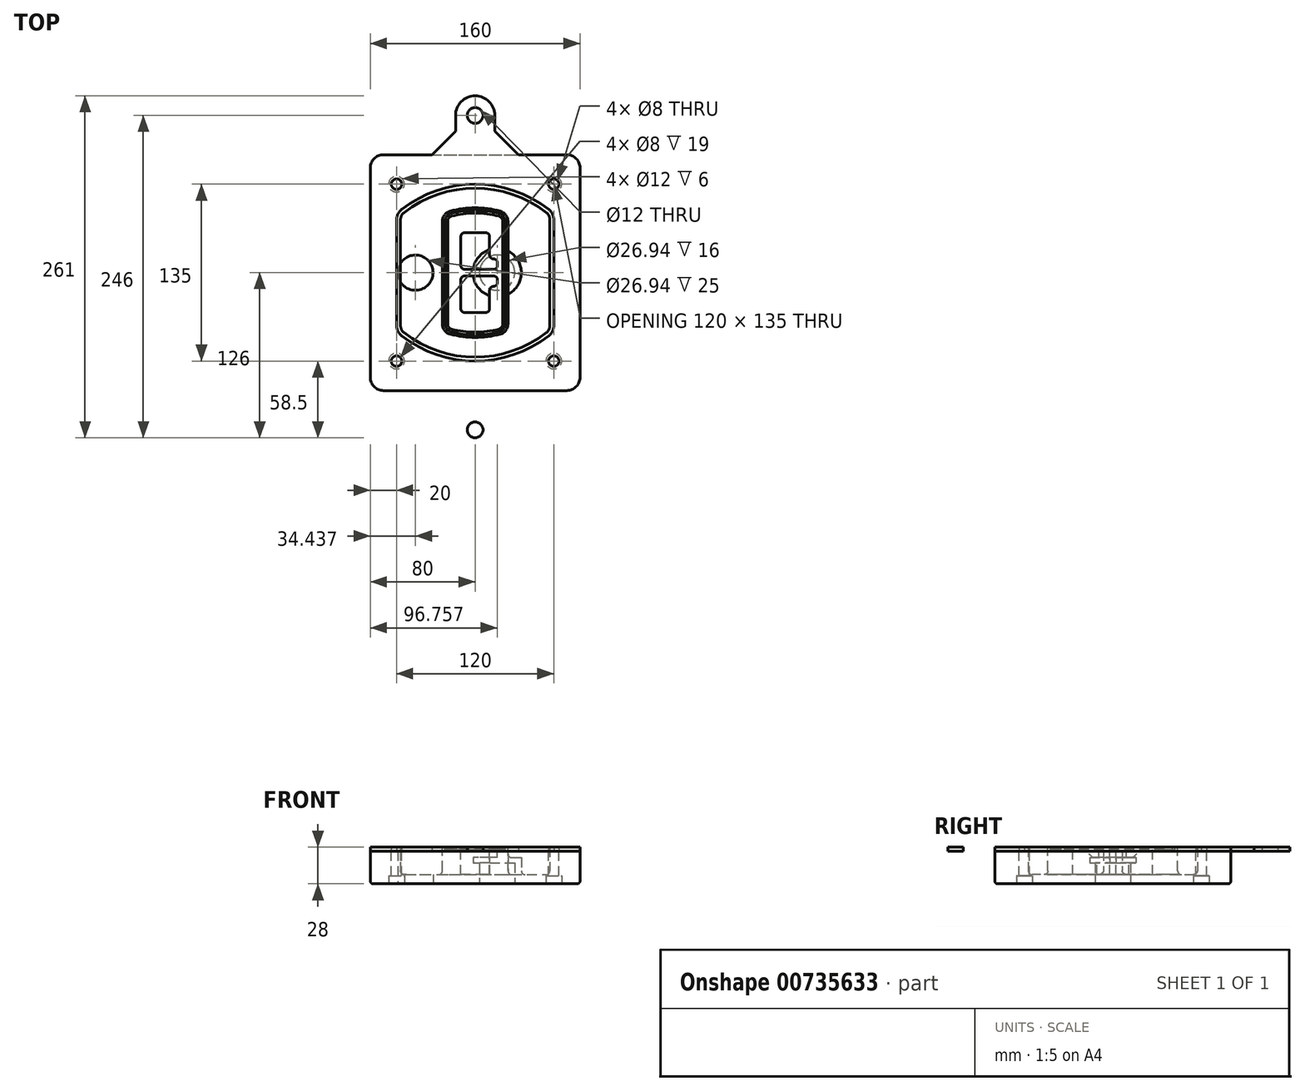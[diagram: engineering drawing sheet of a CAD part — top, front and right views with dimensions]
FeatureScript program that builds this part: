
annotation { "Feature Type Name" : "Feature", "Feature Type Description" : "" }
export const myFeature = defineFeature(function(context is Context, id is Id, definition is map)
    precondition{}
    {
        {
            var Q0;
            Q0=qCreatedBy(makeId("Top.planeOp"),FACE);
            var sketch = newSketch(context, id + "F0", { "sketchPlane" : qUnion([Q0])});
            skPoint(sketch, "E0.rect.middle", {"position": v(0, 0) * mm});
            skLineSegment(sketch, "E1.bottom", {"start": v(-70, -90) * mm, "end": v(70, -90) * mm});
            skLineSegment(sketch, "E1.top", {"start": v(-70, 90) * mm, "end": v(70, 90) * mm});
            skLineSegment(sketch, "E1.left", {"start": v(-80, -80) * mm, "end": v(-80, 80) * mm});
            skLineSegment(sketch, "E1.right", {"start": v(80, -80) * mm, "end": v(80, 80) * mm});
            skLineSegment(sketch, "E2", {"start": v(-80, 90) * mm, "end": v(80, -90) * mm, "construction": true});
            skLineSegment(sketch, "E3", {"start": v(80, 90) * mm, "end": v(-80, -90) * mm, "construction": true});
            skCircle(sketch, "E4", {"center": v(-60, 67.5) * mm, "radius": 4 * mm});
            skCircle(sketch, "E5", {"center": v(60, 67.5) * mm, "radius": 4 * mm});
            skCircle(sketch, "E6", {"center": v(60, -67.5) * mm, "radius": 4 * mm});
            skCircle(sketch, "E7", {"center": v(-60, -67.5) * mm, "radius": 4 * mm});
            skLineSegment(sketch, "E8", {"start": v(-60, 67.5) * mm, "end": v(60, 67.5) * mm, "construction": true});
            skLineSegment(sketch, "E9", {"start": v(60, 67.5) * mm, "end": v(60, -67.5) * mm, "construction": true});
            skLineSegment(sketch, "E10", {"start": v(60, -67.5) * mm, "end": v(-60, -67.5) * mm, "construction": true});
            skLineSegment(sketch, "E11", {"start": v(-60, -67.5) * mm, "end": v(-60, 67.5) * mm, "construction": true});
            skLineSegment(sketch, "E12", {"start": v(-60, 40.3) * mm, "end": v(-60, -40.3) * mm});
            skLineSegment(sketch, "E13", {"start": v(60, 40.3) * mm, "end": v(60, -40.3) * mm});
            skArc(sketch, "E14", {"start": v(56.15, 48.18) * mm, "mid": v(0, 67.5) * mm, "end": v(-56.15, 48.18) * mm});
            skArc(sketch, "E15", {"start": v(-56.15, -48.18) * mm, "mid": v(0, -67.5) * mm, "end": v(56.15, -48.18) * mm});
            skLineSegment(sketch, "E16", {"start": v(-60, 0) * mm, "end": v(60, 0) * mm, "construction": true});
            skPoint(sketch, "E17.visualSharp", {"position": v(-60, -45) * mm});
            skArc(sketch, "E17.filletArc", {"start": v(-60, -40.3) * mm, "mid": v(-58.99, -44.68) * mm, "end": v(-56.15, -48.18) * mm});
            skPoint(sketch, "E18.visualSharp", {"position": v(-60, 45) * mm});
            skArc(sketch, "E18.filletArc", {"start": v(-56.15, 48.18) * mm, "mid": v(-58.99, 44.68) * mm, "end": v(-60, 40.3) * mm});
            skPoint(sketch, "E19.visualSharp", {"position": v(60, 45) * mm});
            skArc(sketch, "E19.filletArc", {"start": v(60, 40.3) * mm, "mid": v(58.99, 44.68) * mm, "end": v(56.15, 48.18) * mm});
            skPoint(sketch, "E20.visualSharp", {"position": v(60, -45) * mm});
            skArc(sketch, "E20.filletArc", {"start": v(56.15, -48.18) * mm, "mid": v(58.99, -44.68) * mm, "end": v(60, -40.3) * mm});
            skPoint(sketch, "E21.visualSharp", {"position": v(-80, 90) * mm});
            skArc(sketch, "E21.filletArc", {"start": v(-70, 90) * mm, "mid": v(-77.07, 87.07) * mm, "end": v(-80, 80) * mm});
            skPoint(sketch, "E22.visualSharp", {"position": v(80, 90) * mm});
            skArc(sketch, "E22.filletArc", {"start": v(80, 80) * mm, "mid": v(77.07, 87.07) * mm, "end": v(70, 90) * mm});
            skPoint(sketch, "E23.visualSharp", {"position": v(80, -90) * mm});
            skArc(sketch, "E23.filletArc", {"start": v(70, -90) * mm, "mid": v(77.07, -87.07) * mm, "end": v(80, -80) * mm});
            skPoint(sketch, "E24.visualSharp", {"position": v(-80, -90) * mm});
            skArc(sketch, "E24.filletArc", {"start": v(-80, -80) * mm, "mid": v(-77.07, -87.07) * mm, "end": v(-70, -90) * mm});
            skArc(sketch, "E25.0", {"start": v(57, 40.3) * mm, "mid": v(56.3, 43.36) * mm, "end": v(54.3, 45.81) * mm});
            skLineSegment(sketch, "E25.1", {"start": v(57, 40.3) * mm, "end": v(57, -40.3) * mm});
            skArc(sketch, "E25.2", {"start": v(54.3, -45.81) * mm, "mid": v(56.3, -43.36) * mm, "end": v(57, -40.3) * mm});
            skArc(sketch, "E25.3", {"start": v(-54.3, -45.81) * mm, "mid": v(0, -64.5) * mm, "end": v(54.3, -45.81) * mm});
            skArc(sketch, "E25.4", {"start": v(-57, -40.3) * mm, "mid": v(-56.3, -43.36) * mm, "end": v(-54.3, -45.81) * mm});
            skArc(sketch, "E25.5", {"start": v(54.3, 45.81) * mm, "mid": v(0, 64.5) * mm, "end": v(-54.3, 45.81) * mm});
            skLineSegment(sketch, "E25.6", {"start": v(-57, 40.3) * mm, "end": v(-57, -40.3) * mm});
            skArc(sketch, "E25.7", {"start": v(-54.3, 45.81) * mm, "mid": v(-56.3, 43.36) * mm, "end": v(-57, 40.3) * mm});
            skArc(sketch, "E26.0", {"start": v(-58.62, 51.33) * mm, "mid": v(-62.58, 46.43) * mm, "end": v(-64, 40.3) * mm});
            skArc(sketch, "E26.1", {"start": v(58.62, 51.33) * mm, "mid": v(0, 71.5) * mm, "end": v(-58.62, 51.33) * mm});
            skArc(sketch, "E26.2", {"start": v(64, 40.3) * mm, "mid": v(62.58, 46.43) * mm, "end": v(58.62, 51.33) * mm});
            skLineSegment(sketch, "E26.3", {"start": v(64, 40.3) * mm, "end": v(64, -40.3) * mm});
            skArc(sketch, "E26.4", {"start": v(58.62, -51.33) * mm, "mid": v(62.58, -46.43) * mm, "end": v(64, -40.3) * mm});
            skLineSegment(sketch, "E26.5", {"start": v(-64, 40.3) * mm, "end": v(-64, -40.3) * mm});
            skArc(sketch, "E26.6", {"start": v(-58.62, -51.33) * mm, "mid": v(0, -71.5) * mm, "end": v(58.62, -51.33) * mm});
            skArc(sketch, "E26.7", {"start": v(-64, -40.3) * mm, "mid": v(-62.58, -46.43) * mm, "end": v(-58.62, -51.33) * mm});
            skSolve(sketch);
        }
        {
            var Q0;
            Q0=makeQuery(id+"F0.imprint","IMPRINT",FACE,{"disambiguationData":[TD([[makeQuery(id+"F0.imprint","IMPRINT",EDGE,{"derivedFrom":sQuery(id+"F0.wireOp",EDGE,"E1.bottom")}),1.0]])]});
            var Q1;
            Q1=makeQuery(id+"F0.imprint","IMPRINT",FACE,{"disambiguationData":[TD([[makeQuery(id+"F0.imprint","IMPRINT",EDGE,{"derivedFrom":sQuery(id+"F0.wireOp",EDGE,"E12")}),1.0]])]});
            var Q2;
            Q2=makeQuery(id+"F0.imprint","IMPRINT",FACE,{"disambiguationData":[TD([[makeQuery(id+"F0.imprint","IMPRINT",EDGE,{"derivedFrom":sQuery(id+"F0.wireOp",EDGE,"E25.0")}),1.0]])]});
            var Q3;
            Q3=makeQuery(id+"F0.imprint","IMPRINT",FACE,{"disambiguationData":[TD([[makeQuery(id+"F0.imprint","IMPRINT",EDGE,{"derivedFrom":sQuery(id+"F0.wireOp",EDGE,"E12")}),-1.0]])]});
            extrude(context, id + "F1", {"entities" : qUnion([Q0, Q1, Q2, Q3]), "oppositeDirection" : true, "depth" : 25 * mm});
        }
        {
            var Q0;
            Q0=makeQuery(id+"F0.imprint","IMPRINT",FACE,{"disambiguationData":[TD([[makeQuery(id+"F0.imprint","IMPRINT",EDGE,{"derivedFrom":sQuery(id+"F0.wireOp",EDGE,"E12")}),1.0]])]});
            extrude(context, id + "F2", {"entities" : qUnion([Q0]), "operationType" : NewBodyOperationType.ADD, "depth" : 3 * mm});
        }
        {
            var Q0;
            Q0=makeQuery(id+"F0.imprint","IMPRINT",FACE,{"disambiguationData":[TD([[makeQuery(id+"F0.imprint","IMPRINT",EDGE,{"derivedFrom":sQuery(id+"F0.wireOp",EDGE,"E25.0")}),1.0]])]});
            extrude(context, id + "F3", {"entities" : qUnion([Q0]), "operationType" : NewBodyOperationType.REMOVE, "oppositeDirection" : true, "depth" : 18 * mm});
        }
        {
            var Q0;
            Q0=makeQuery(id+"F2.opExtrude","CAP_FACE",FACE,{"disambiguationData":[OSD([sQuery(id+"F0.wireOp",EDGE,"E12"),sQuery(id+"F0.wireOp",EDGE,"E13"),sQuery(id+"F0.wireOp",EDGE,"E14"),sQuery(id+"F0.wireOp",EDGE,"E15"),sQuery(id+"F0.wireOp",EDGE,"E17.filletArc"),sQuery(id+"F0.wireOp",EDGE,"E18.filletArc"),sQuery(id+"F0.wireOp",EDGE,"E19.filletArc"),sQuery(id+"F0.wireOp",EDGE,"E20.filletArc"),sQuery(id+"F0.wireOp",EDGE,"E25.0"),sQuery(id+"F0.wireOp",EDGE,"E25.1"),sQuery(id+"F0.wireOp",EDGE,"E25.2"),sQuery(id+"F0.wireOp",EDGE,"E25.3"),sQuery(id+"F0.wireOp",EDGE,"E25.4"),sQuery(id+"F0.wireOp",EDGE,"E25.5"),sQuery(id+"F0.wireOp",EDGE,"E25.6"),sQuery(id+"F0.wireOp",EDGE,"E25.7")])],"isStart":false});
            var sketch = newSketch(context, id + "F4", { "sketchPlane" : qUnion([Q0])});
            skArc(sketch, "E27.0", {"start": v(-19.08, -46.97) * mm, "mid": v(0, -49.5) * mm, "end": v(19.08, -46.97) * mm});
            skArc(sketch, "E28.0", {"start": v(19.08, 46.97) * mm, "mid": v(0, 49.5) * mm, "end": v(-19.08, 46.97) * mm});
            skLineSegment(sketch, "E29", {"start": v(-25, 39.25) * mm, "end": v(-25, -39.25) * mm});
            skLineSegment(sketch, "E30", {"start": v(25, 39.25) * mm, "end": v(25, -39.25) * mm});
            skLineSegment(sketch, "E31", {"start": v(-25, 45.1) * mm, "end": v(25, 45.1) * mm, "construction": true});
            skLineSegment(sketch, "E32", {"start": v(-25, -45.1) * mm, "end": v(25, -45.1) * mm, "construction": true});
            skPoint(sketch, "E33.visualSharp", {"position": v(-25, 45.1) * mm});
            skArc(sketch, "E33.filletArc", {"start": v(-19.08, 46.97) * mm, "mid": v(-23.35, 44.11) * mm, "end": v(-25, 39.25) * mm});
            skPoint(sketch, "E34.visualSharp", {"position": v(25, 45.1) * mm});
            skArc(sketch, "E34.filletArc", {"start": v(25, 39.25) * mm, "mid": v(23.35, 44.11) * mm, "end": v(19.08, 46.97) * mm});
            skPoint(sketch, "E35.visualSharp", {"position": v(25, -45.1) * mm});
            skArc(sketch, "E35.filletArc", {"start": v(19.08, -46.97) * mm, "mid": v(23.35, -44.11) * mm, "end": v(25, -39.25) * mm});
            skPoint(sketch, "E36.visualSharp", {"position": v(-25, -45.1) * mm});
            skArc(sketch, "E36.filletArc", {"start": v(-25, -39.25) * mm, "mid": v(-23.35, -44.11) * mm, "end": v(-19.08, -46.97) * mm});
            skArc(sketch, "E37.0", {"start": v(54.3, 45.81) * mm, "mid": v(0, 64.5) * mm, "end": v(-54.3, 45.81) * mm});
            skArc(sketch, "E37.1", {"start": v(-54.3, 45.81) * mm, "mid": v(-56.3, 43.36) * mm, "end": v(-57, 40.3) * mm});
            skLineSegment(sketch, "E37.2", {"start": v(-57, 40.3) * mm, "end": v(-57, -40.3) * mm});
            skArc(sketch, "E37.3", {"start": v(-57, -40.3) * mm, "mid": v(-56.3, -43.36) * mm, "end": v(-54.3, -45.81) * mm});
            skArc(sketch, "E37.4", {"start": v(-54.3, -45.81) * mm, "mid": v(0, -64.5) * mm, "end": v(54.3, -45.81) * mm});
            skArc(sketch, "E37.5", {"start": v(54.3, -45.81) * mm, "mid": v(56.3, -43.36) * mm, "end": v(57, -40.3) * mm});
            skLineSegment(sketch, "E37.6", {"start": v(57, 40.3) * mm, "end": v(57, -40.3) * mm});
            skArc(sketch, "E37.7", {"start": v(57, 40.3) * mm, "mid": v(56.3, 43.36) * mm, "end": v(54.3, 45.81) * mm});
            skLineSegment(sketch, "E38.0", {"start": v(23, 39.25) * mm, "end": v(23, -39.25) * mm});
            skArc(sketch, "E38.1", {"start": v(18.56, -45.04) * mm, "mid": v(21.76, -42.9) * mm, "end": v(23, -39.25) * mm});
            skArc(sketch, "E38.2", {"start": v(-18.56, -45.04) * mm, "mid": v(0, -47.5) * mm, "end": v(18.56, -45.04) * mm});
            skArc(sketch, "E38.3", {"start": v(-23, -39.25) * mm, "mid": v(-21.76, -42.9) * mm, "end": v(-18.56, -45.04) * mm});
            skLineSegment(sketch, "E38.4", {"start": v(-23, 39.25) * mm, "end": v(-23, -39.25) * mm});
            skArc(sketch, "E38.5", {"start": v(23, 39.25) * mm, "mid": v(21.76, 42.9) * mm, "end": v(18.56, 45.04) * mm});
            skArc(sketch, "E38.6", {"start": v(-18.56, 45.04) * mm, "mid": v(-21.76, 42.9) * mm, "end": v(-23, 39.25) * mm});
            skArc(sketch, "E38.7", {"start": v(18.56, 45.04) * mm, "mid": v(0, 47.5) * mm, "end": v(-18.56, 45.04) * mm});
            skArc(sketch, "E39.0", {"start": v(21, 39.25) * mm, "mid": v(20.18, 41.68) * mm, "end": v(18.04, 43.1) * mm});
            skLineSegment(sketch, "E39.1", {"start": v(21, 39.25) * mm, "end": v(21, -39.25) * mm});
            skArc(sketch, "E39.2", {"start": v(18.04, -43.1) * mm, "mid": v(20.18, -41.68) * mm, "end": v(21, -39.25) * mm});
            skArc(sketch, "E39.3", {"start": v(-18.04, -43.1) * mm, "mid": v(0, -45.5) * mm, "end": v(18.04, -43.1) * mm});
            skArc(sketch, "E39.4", {"start": v(-21, -39.25) * mm, "mid": v(-20.18, -41.68) * mm, "end": v(-18.04, -43.1) * mm});
            skArc(sketch, "E39.5", {"start": v(18.04, 43.1) * mm, "mid": v(0, 45.5) * mm, "end": v(-18.04, 43.1) * mm});
            skLineSegment(sketch, "E39.6", {"start": v(-21, 39.25) * mm, "end": v(-21, -39.25) * mm});
            skArc(sketch, "E39.7", {"start": v(-18.04, 43.1) * mm, "mid": v(-20.18, 41.68) * mm, "end": v(-21, 39.25) * mm});
            skLineSegment(sketch, "E40", {"start": v(-25, 0) * mm, "end": v(25, 0) * mm, "construction": true});
            skLineSegment(sketch, "E41", {"start": v(-11, 5.5) * mm, "end": v(-11, 27.5) * mm});
            skLineSegment(sketch, "E42", {"start": v(-8, 30.5) * mm, "end": v(8, 30.5) * mm});
            skLineSegment(sketch, "E43", {"start": v(11, 27.5) * mm, "end": v(11, 13.5) * mm});
            skLineSegment(sketch, "E44", {"start": v(14, 10.5) * mm, "end": v(14, 10.5) * mm});
            skLineSegment(sketch, "E45", {"start": v(17, 7.5) * mm, "end": v(17, 5.5) * mm});
            skLineSegment(sketch, "E46", {"start": v(14, 2.5) * mm, "end": v(-8, 2.5) * mm});
            skPoint(sketch, "E47.visualSharp", {"position": v(-11, 30.5) * mm});
            skArc(sketch, "E47.filletArc", {"start": v(-8, 30.5) * mm, "mid": v(-10.12, 29.62) * mm, "end": v(-11, 27.5) * mm});
            skPoint(sketch, "E48.visualSharp", {"position": v(11, 30.5) * mm});
            skArc(sketch, "E48.filletArc", {"start": v(11, 27.5) * mm, "mid": v(10.12, 29.62) * mm, "end": v(8, 30.5) * mm});
            skPoint(sketch, "E49.visualSharp", {"position": v(11, 10.5) * mm});
            skArc(sketch, "E49.filletArc", {"start": v(11, 13.5) * mm, "mid": v(11.88, 11.38) * mm, "end": v(14, 10.5) * mm});
            skPoint(sketch, "E50.visualSharp", {"position": v(17, 10.5) * mm});
            skArc(sketch, "E50.filletArc", {"start": v(17, 7.5) * mm, "mid": v(16.12, 9.62) * mm, "end": v(14, 10.5) * mm});
            skPoint(sketch, "E51.visualSharp", {"position": v(17, 2.5) * mm});
            skArc(sketch, "E51.filletArc", {"start": v(14, 2.5) * mm, "mid": v(16.12, 3.38) * mm, "end": v(17, 5.5) * mm});
            skPoint(sketch, "E52.visualSharp", {"position": v(-11, 2.5) * mm});
            skArc(sketch, "E52.filletArc", {"start": v(-11, 5.5) * mm, "mid": v(-10.12, 3.38) * mm, "end": v(-8, 2.5) * mm});
            skLineSegment(sketch, "E53.0.MirrorCS", {"start": v(14, -2.5) * mm, "end": v(-8, -2.5) * mm});
            skArc(sketch, "E54.0.MirrorCS", {"start": v(-11, -5.5) * mm, "mid": v(-10.12, -3.38) * mm, "end": v(-8, -2.5) * mm});
            skLineSegment(sketch, "E55.0.MirrorCS", {"start": v(-11, -5.5) * mm, "end": v(-11, -27.5) * mm});
            skArc(sketch, "E56.0.MirrorCS", {"start": v(-8, -30.5) * mm, "mid": v(-10.12, -29.62) * mm, "end": v(-11, -27.5) * mm});
            skLineSegment(sketch, "E57.0.MirrorCS", {"start": v(-8, -30.5) * mm, "end": v(8, -30.5) * mm});
            skArc(sketch, "E58.0.MirrorCS", {"start": v(11, -27.5) * mm, "mid": v(10.12, -29.62) * mm, "end": v(8, -30.5) * mm});
            skLineSegment(sketch, "E59.0.MirrorCS", {"start": v(11, -27.5) * mm, "end": v(11, -13.5) * mm});
            skArc(sketch, "E60.0.MirrorCS", {"start": v(11, -13.5) * mm, "mid": v(11.88, -11.38) * mm, "end": v(14, -10.5) * mm});
            skArc(sketch, "E61.0.MirrorCS", {"start": v(17, -7.5) * mm, "mid": v(16.12, -9.62) * mm, "end": v(14, -10.5) * mm});
            skLineSegment(sketch, "E62.0.MirrorCS", {"start": v(17, -7.5) * mm, "end": v(17, -5.5) * mm});
            skArc(sketch, "E63.0.MirrorCS", {"start": v(14, -2.5) * mm, "mid": v(16.12, -3.38) * mm, "end": v(17, -5.5) * mm});
            skSolve(sketch);
        }
        {
            var Q0;
            Q0=makeQuery(id+"F4.imprint","IMPRINT",FACE,{"disambiguationData":[TD([[makeQuery(id+"F4.imprint","IMPRINT",EDGE,{"derivedFrom":sQuery(id+"F4.wireOp",EDGE,"E27.0")}),1.0]])]});
            var Q1;
            Q1=makeQuery(id+"F4.imprint","IMPRINT",FACE,{"disambiguationData":[TD([[makeQuery(id+"F4.imprint","IMPRINT",EDGE,{"derivedFrom":sQuery(id+"F4.wireOp",EDGE,"E38.0")}),-1.0]])]});
            var Q2;
            Q2=makeQuery(id+"F4.imprint","IMPRINT",FACE,{"disambiguationData":[TD([[makeQuery(id+"F4.imprint","IMPRINT",EDGE,{"derivedFrom":sQuery(id+"F4.wireOp",EDGE,"E39.0")}),1.0]])]});
            extrude(context, id + "F5", {"entities" : qUnion([Q0, Q1, Q2]), "operationType" : NewBodyOperationType.ADD, "endBound" : BoundingType.UP_TO_NEXT, "oppositeDirection" : true, "depth" : 25 * mm});
        }
        {
            var Q0;
            Q0=makeQuery(id+"F4.imprint","IMPRINT",FACE,{"disambiguationData":[TD([[makeQuery(id+"F4.imprint","IMPRINT",EDGE,{"derivedFrom":sQuery(id+"F4.wireOp",EDGE,"E38.0")}),-1.0]])]});
            extrude(context, id + "F6", {"entities" : qUnion([Q0]), "operationType" : NewBodyOperationType.REMOVE, "oppositeDirection" : true, "depth" : 2 * mm});
        }
        {
            var Q0;
            Q0=makeQuery(id+"F1.opExtrude","CAP_FACE",FACE,{"disambiguationData":[OSD([sQuery(id+"F0.wireOp",EDGE,"E1.bottom"),sQuery(id+"F0.wireOp",EDGE,"E1.top"),sQuery(id+"F0.wireOp",EDGE,"E1.left"),sQuery(id+"F0.wireOp",EDGE,"E1.right"),sQuery(id+"F0.wireOp",EDGE,"E4"),sQuery(id+"F0.wireOp",EDGE,"E5"),sQuery(id+"F0.wireOp",EDGE,"E6"),sQuery(id+"F0.wireOp",EDGE,"E7"),sQuery(id+"F0.wireOp",EDGE,"E21.filletArc"),sQuery(id+"F0.wireOp",EDGE,"E22.filletArc"),sQuery(id+"F0.wireOp",EDGE,"E23.filletArc"),sQuery(id+"F0.wireOp",EDGE,"E24.filletArc")])],"isStart":false});
            var sketch = newSketch(context, id + "F7", { "sketchPlane" : qUnion([Q0])});
            skCircle(sketch, "E64", {"center": v(16.76, 0) * mm, "radius": 13.47 * mm});
            skCircle(sketch, "E65", {"center": v(-45.56, 0) * mm, "radius": 13.47 * mm});
            skLineSegment(sketch, "E66", {"start": v(80, 0) * mm, "end": v(-80, 0) * mm});
            skCircle(sketch, "E67", {"center": v(16.76, 0) * mm, "radius": 18.47 * mm});
            skCircle(sketch, "E68", {"center": v(60, -67.5) * mm, "radius": 6 * mm});
            skCircle(sketch, "E69", {"center": v(-60, -67.5) * mm, "radius": 6 * mm});
            skCircle(sketch, "E70", {"center": v(-60, 67.5) * mm, "radius": 6 * mm});
            skCircle(sketch, "E71", {"center": v(60, 67.5) * mm, "radius": 6 * mm});
            skSolve(sketch);
        }
        {
            var Q0;
            {var subQ1=sQuery(id+"F7.wireOp",EDGE,"E66");var subQ4=sQuery(id+"F7.wireOp",EDGE,"E64");var subQ6=makeQuery(id+"F7.imprint","INTERSECT",VERTEX,{"disambiguationData":[OD(0.0)],"derivedFrom":[subQ4,subQ1]});Q0=makeQuery(id+"F7.imprint","IMPRINT",FACE,{"disambiguationData":[TD([[makeQuery(id+"F7.imprint","IMPRINT",EDGE,{"disambiguationData":[TD([[subQ6,-1.0]])],"derivedFrom":subQ4}),-1.0]])]});}
            var Q1;
            {var subQ0=sQuery(id+"F7.wireOp",EDGE,"E66");var subQ1=sQuery(id+"F7.wireOp",EDGE,"E64");var subQ3=makeQuery(id+"F7.imprint","INTERSECT",VERTEX,{"disambiguationData":[OD(0.0)],"derivedFrom":[subQ1,subQ0]});Q1=makeQuery(id+"F7.imprint","IMPRINT",FACE,{"disambiguationData":[TD([[makeQuery(id+"F7.imprint","IMPRINT",EDGE,{"disambiguationData":[TD([[subQ3,-1.0]])],"derivedFrom":subQ1}),1.0]])]});}
            var Q2;
            {var subQ0=sQuery(id+"F7.wireOp",EDGE,"E66");var subQ1=sQuery(id+"F7.wireOp",EDGE,"E64");var subQ3=makeQuery(id+"F7.imprint","INTERSECT",VERTEX,{"disambiguationData":[OD(0.0)],"derivedFrom":[subQ1,subQ0]});Q2=makeQuery(id+"F7.imprint","IMPRINT",FACE,{"disambiguationData":[TD([[makeQuery(id+"F7.imprint","IMPRINT",EDGE,{"disambiguationData":[TD([[subQ3,1.0]])],"derivedFrom":subQ1}),1.0]])]});}
            var Q3;
            {var subQ1=sQuery(id+"F7.wireOp",EDGE,"E66");var subQ4=sQuery(id+"F7.wireOp",EDGE,"E64");var subQ6=makeQuery(id+"F7.imprint","INTERSECT",VERTEX,{"disambiguationData":[OD(0.0)],"derivedFrom":[subQ4,subQ1]});Q3=makeQuery(id+"F7.imprint","IMPRINT",FACE,{"disambiguationData":[TD([[makeQuery(id+"F7.imprint","IMPRINT",EDGE,{"disambiguationData":[TD([[subQ6,1.0]])],"derivedFrom":subQ4}),-1.0]])]});}
            extrude(context, id + "F8", {"entities" : qUnion([Q0, Q1, Q2, Q3]), "operationType" : NewBodyOperationType.ADD, "oppositeDirection" : true, "depth" : 20 * mm});
        }
        {
            var Q0;
            {var subQ0=sQuery(id+"F7.wireOp",EDGE,"E66");var subQ1=sQuery(id+"F7.wireOp",EDGE,"E64");var subQ3=makeQuery(id+"F7.imprint","INTERSECT",VERTEX,{"disambiguationData":[OD(0.0)],"derivedFrom":[subQ1,subQ0]});Q0=makeQuery(id+"F7.imprint","IMPRINT",FACE,{"disambiguationData":[TD([[makeQuery(id+"F7.imprint","IMPRINT",EDGE,{"disambiguationData":[TD([[subQ3,-1.0]])],"derivedFrom":subQ1}),1.0]])]});}
            var Q1;
            {var subQ0=sQuery(id+"F7.wireOp",EDGE,"E66");var subQ1=sQuery(id+"F7.wireOp",EDGE,"E64");var subQ3=makeQuery(id+"F7.imprint","INTERSECT",VERTEX,{"disambiguationData":[OD(0.0)],"derivedFrom":[subQ1,subQ0]});Q1=makeQuery(id+"F7.imprint","IMPRINT",FACE,{"disambiguationData":[TD([[makeQuery(id+"F7.imprint","IMPRINT",EDGE,{"disambiguationData":[TD([[subQ3,1.0]])],"derivedFrom":subQ1}),1.0]])]});}
            extrude(context, id + "F9", {"entities" : qUnion([Q0, Q1]), "operationType" : NewBodyOperationType.REMOVE, "oppositeDirection" : true, "depth" : 16 * mm});
        }
        {
            var Q0;
            {var subQ0=sQuery(id+"F7.wireOp",EDGE,"E66");var subQ1=sQuery(id+"F7.wireOp",EDGE,"E65");var subQ3=makeQuery(id+"F7.imprint","INTERSECT",VERTEX,{"disambiguationData":[OD(0.0)],"derivedFrom":[subQ1,subQ0]});Q0=makeQuery(id+"F7.imprint","IMPRINT",FACE,{"disambiguationData":[TD([[makeQuery(id+"F7.imprint","IMPRINT",EDGE,{"disambiguationData":[TD([[subQ3,-1.0]])],"derivedFrom":subQ1}),1.0]])]});}
            var Q1;
            {var subQ0=sQuery(id+"F7.wireOp",EDGE,"E66");var subQ1=sQuery(id+"F7.wireOp",EDGE,"E65");var subQ3=makeQuery(id+"F7.imprint","INTERSECT",VERTEX,{"disambiguationData":[OD(0.0)],"derivedFrom":[subQ1,subQ0]});Q1=makeQuery(id+"F7.imprint","IMPRINT",FACE,{"disambiguationData":[TD([[makeQuery(id+"F7.imprint","IMPRINT",EDGE,{"disambiguationData":[TD([[subQ3,1.0]])],"derivedFrom":subQ1}),1.0]])]});}
            extrude(context, id + "F10", {"entities" : qUnion([Q0, Q1]), "operationType" : NewBodyOperationType.REMOVE, "oppositeDirection" : true, "depth" : 25 * mm});
        }
        {
            var Q0;
            Q0=makeQuery(id+"F7.imprint","IMPRINT",FACE,{"disambiguationData":[TD([[makeQuery(id+"F7.imprint","IMPRINT",EDGE,{"derivedFrom":sQuery(id+"F7.wireOp",EDGE,"E68")}),1.0]])]});
            var Q1;
            Q1=makeQuery(id+"F7.imprint","IMPRINT",FACE,{"disambiguationData":[TD([[makeQuery(id+"F7.imprint","IMPRINT",EDGE,{"derivedFrom":makeQuery(id+"F1.opExtrude","CAP_EDGE",EDGE,{"disambiguationData":[OSD([sQuery(id+"F0.wireOp",EDGE,"E5")])],"isStart":false})}),-1.0]])]});
            var Q2;
            Q2=makeQuery(id+"F7.imprint","IMPRINT",FACE,{"disambiguationData":[TD([[makeQuery(id+"F7.imprint","IMPRINT",EDGE,{"derivedFrom":sQuery(id+"F7.wireOp",EDGE,"E69")}),1.0]])]});
            var Q3;
            Q3=makeQuery(id+"F7.imprint","IMPRINT",FACE,{"disambiguationData":[TD([[makeQuery(id+"F7.imprint","IMPRINT",EDGE,{"derivedFrom":makeQuery(id+"F1.opExtrude","CAP_EDGE",EDGE,{"disambiguationData":[OSD([sQuery(id+"F0.wireOp",EDGE,"E4")])],"isStart":false})}),-1.0]])]});
            var Q4;
            Q4=makeQuery(id+"F7.imprint","IMPRINT",FACE,{"disambiguationData":[TD([[makeQuery(id+"F7.imprint","IMPRINT",EDGE,{"derivedFrom":sQuery(id+"F7.wireOp",EDGE,"E70")}),1.0]])]});
            var Q5;
            Q5=makeQuery(id+"F7.imprint","IMPRINT",FACE,{"disambiguationData":[TD([[makeQuery(id+"F7.imprint","IMPRINT",EDGE,{"derivedFrom":makeQuery(id+"F1.opExtrude","CAP_EDGE",EDGE,{"disambiguationData":[OSD([sQuery(id+"F0.wireOp",EDGE,"E7")])],"isStart":false})}),-1.0]])]});
            var Q6;
            Q6=makeQuery(id+"F7.imprint","IMPRINT",FACE,{"disambiguationData":[TD([[makeQuery(id+"F7.imprint","IMPRINT",EDGE,{"derivedFrom":sQuery(id+"F7.wireOp",EDGE,"E71")}),1.0]])]});
            var Q7;
            Q7=makeQuery(id+"F7.imprint","IMPRINT",FACE,{"disambiguationData":[TD([[makeQuery(id+"F7.imprint","IMPRINT",EDGE,{"derivedFrom":makeQuery(id+"F1.opExtrude","CAP_EDGE",EDGE,{"disambiguationData":[OSD([sQuery(id+"F0.wireOp",EDGE,"E6")])],"isStart":false})}),-1.0]])]});
            extrude(context, id + "F11", {"entities" : qUnion([Q0, Q1, Q2, Q3, Q4, Q5, Q6, Q7]), "operationType" : NewBodyOperationType.REMOVE, "oppositeDirection" : true, "depth" : 6 * mm});
        }
        {
            var Q0;
            Q0=makeQuery(id+"F9.boolean.opBoolean","COPY",FACE,{"derivedFrom":makeQuery(id+"F9.opExtrude","CAP_FACE",FACE,{"disambiguationData":[OSD([sQuery(id+"F7.wireOp",EDGE,"E64")])],"isStart":false})});
            var sketch = newSketch(context, id + "F12", { "sketchPlane" : qUnion([Q0])});
            skArc(sketch, "E72.0", {"start": v(11, 17.55) * mm, "mid": v(2.57, 11.82) * mm, "end": v(-1.54, 2.5) * mm});
            skArc(sketch, "E72.1", {"start": v(-1.54, -2.5) * mm, "mid": v(2.57, -11.82) * mm, "end": v(11, -17.55) * mm});
            skLineSegment(sketch, "E73", {"start": v(-1.54, -2.5) * mm, "end": v(14, -2.5) * mm});
            skLineSegment(sketch, "E74.0", {"start": v(14, 2.5) * mm, "end": v(-1.54, 2.5) * mm});
            skArc(sketch, "E74.1", {"start": v(14, 2.5) * mm, "mid": v(16.12, 3.38) * mm, "end": v(17, 5.5) * mm});
            skLineSegment(sketch, "E74.2", {"start": v(17, 7.5) * mm, "end": v(17, 5.5) * mm});
            skArc(sketch, "E74.3", {"start": v(17, 7.5) * mm, "mid": v(16.12, 9.62) * mm, "end": v(14, 10.5) * mm});
            skArc(sketch, "E74.4", {"start": v(11, 13.5) * mm, "mid": v(11.88, 11.38) * mm, "end": v(14, 10.5) * mm});
            skLineSegment(sketch, "E74.5", {"start": v(11, 17.55) * mm, "end": v(11, 13.5) * mm});
            skLineSegment(sketch, "E74.7", {"start": v(14, -2.5) * mm, "end": v(-1.54, -2.5) * mm});
            skArc(sketch, "E74.8", {"start": v(14, -2.5) * mm, "mid": v(16.12, -3.38) * mm, "end": v(17, -5.5) * mm});
            skLineSegment(sketch, "E74.9", {"start": v(17, -7.5) * mm, "end": v(17, -5.5) * mm});
            skArc(sketch, "E74.10", {"start": v(17, -7.5) * mm, "mid": v(16.12, -9.62) * mm, "end": v(14, -10.5) * mm});
            skArc(sketch, "E74.11", {"start": v(11, -13.5) * mm, "mid": v(11.88, -11.38) * mm, "end": v(14, -10.5) * mm});
            skLineSegment(sketch, "E74.12", {"start": v(11, -17.55) * mm, "end": v(11, -13.5) * mm});
            skPoint(sketch, "E75.orphan", {"position": v(11, -27.5) * mm});
            skPoint(sketch, "E76.orphan", {"position": v(-8, -2.5) * mm});
            skPoint(sketch, "E77.orphan", {"position": v(-8, 2.5) * mm});
            skPoint(sketch, "E78.orphan", {"position": v(11, 27.5) * mm});
            skSolve(sketch);
        }
        {
            var Q0;
            {var subQ7=sQuery(id+"F12.wireOp",EDGE,"E72.0");var subQ14=sQuery(id+"F12.wireOp",EDGE,"E72.1");var subQ16=sQuery(id+"F12.wireOp",EDGE,"E74.1");var subQ18=sQuery(id+"F12.wireOp",EDGE,"E74.8");Q0=qUnion([makeQuery(id+"F12.imprint","IMPRINT",FACE,{"disambiguationData":[TD([[makeQuery(id+"F12.imprint","IMPRINT",EDGE,{"derivedFrom":subQ7}),1.0]])]}),makeQuery(id+"F12.imprint","IMPRINT",FACE,{"disambiguationData":[TD([[makeQuery(id+"F12.imprint","IMPRINT",EDGE,{"derivedFrom":subQ14}),1.0]])]}),makeQuery(id+"F12.imprint","IMPRINT",FACE,{"disambiguationData":[TD([[makeQuery(id+"F12.imprint","IMPRINT",EDGE,{"derivedFrom":subQ16}),1.0]])]}),makeQuery(id+"F12.imprint","IMPRINT",FACE,{"disambiguationData":[TD([[makeQuery(id+"F12.imprint","IMPRINT",EDGE,{"derivedFrom":subQ18}),-1.0]])]})]);}
            var Q1;
            Q1=makeQuery(id+"F5.boolean.opBoolean","SPLIT",FACE,{"disambiguationData":[TD([makeQuery(id+"F5.opExtrude","SWEPT_FACE",FACE,{"disambiguationData":[OSD([sQuery(id+"F4.wireOp",EDGE,"E41")])]})])],"derivedFrom":makeQuery(id+"F3.boolean.opBoolean","COPY",FACE,{"derivedFrom":makeQuery(id+"F3.opExtrude","CAP_FACE",FACE,{"disambiguationData":[OSD([sQuery(id+"F0.wireOp",EDGE,"E25.0"),sQuery(id+"F0.wireOp",EDGE,"E25.1"),sQuery(id+"F0.wireOp",EDGE,"E25.2"),sQuery(id+"F0.wireOp",EDGE,"E25.3"),sQuery(id+"F0.wireOp",EDGE,"E25.4"),sQuery(id+"F0.wireOp",EDGE,"E25.5"),sQuery(id+"F0.wireOp",EDGE,"E25.6"),sQuery(id+"F0.wireOp",EDGE,"E25.7")])],"isStart":false})})});
            extrude(context, id + "F13", {"entities" : qUnion([Q0]), "operationType" : NewBodyOperationType.REMOVE, "endBound" : BoundingType.UP_TO_SURFACE, "endBoundEntityFace" : qUnion([Q1]), "depth" : 25 * mm});
        }
        {
            var Q0;
            Q0=makeQuery(id+"F3.boolean.opBoolean","COPY",EDGE,{"derivedFrom":makeQuery(id+"F3.opExtrude","CAP_EDGE",EDGE,{"disambiguationData":[OSD([sQuery(id+"F0.wireOp",EDGE,"E25.6")])],"isStart":false})});
            var Q1;
            Q1=makeQuery(id+"F8.boolean.opBoolean","INTERSECT",EDGE,{"derivedFrom":[makeQuery(id+"F5.opExtrude","SWEPT_FACE",FACE,{"disambiguationData":[OSD([sQuery(id+"F4.wireOp",EDGE,"E30")])]}),makeQuery(id+"F8.opExtrude","CAP_FACE",FACE,{"disambiguationData":[OSD([sQuery(id+"F7.wireOp",EDGE,"E67")])],"isStart":false})]});
            var Q2;
            Q2=makeQuery(id+"F8.boolean.opBoolean","INTERSECT",EDGE,{"disambiguationData":[OD(1.0)],"derivedFrom":[makeQuery(id+"F5.opExtrude","SWEPT_FACE",FACE,{"disambiguationData":[OSD([sQuery(id+"F4.wireOp",EDGE,"E30")])]}),makeQuery(id+"F8.opExtrude","SWEPT_FACE",FACE,{"disambiguationData":[OSD([sQuery(id+"F7.wireOp",EDGE,"E67")])]})]});
            var Q3;
            {var subQ0=sQuery(id+"F4.wireOp",EDGE,"E30");Q3=makeQuery(id+"F8.boolean.opBoolean","SPLIT",EDGE,{"disambiguationData":[TD([makeQuery(id+"F5.opExtrude","SWEPT_FACE",FACE,{"disambiguationData":[OSD([sQuery(id+"F4.wireOp",EDGE,"E35.filletArc")])]})])],"derivedFrom":makeQuery(id+"F5.opExtrude","CAP_EDGE",EDGE,{"disambiguationData":[OSD([subQ0])],"isStart":false})});}
            var Q4;
            {var subQ0=sQuery(id+"F0.wireOp",EDGE,"E25.7");var subQ1=sQuery(id+"F0.wireOp",EDGE,"E25.1");var subQ2=sQuery(id+"F0.wireOp",EDGE,"E25.6");var subQ3=sQuery(id+"F0.wireOp",EDGE,"E25.5");var subQ4=sQuery(id+"F0.wireOp",EDGE,"E25.4");var subQ5=sQuery(id+"F0.wireOp",EDGE,"E25.0");var subQ6=sQuery(id+"F0.wireOp",EDGE,"E25.2");var subQ7=sQuery(id+"F0.wireOp",EDGE,"E25.3");Q4=makeQuery(id+"F8.boolean.opBoolean","INTERSECT",EDGE,{"derivedFrom":[makeQuery(id+"F5.boolean.opBoolean","SPLIT",FACE,{"disambiguationData":[TD([makeQuery(id+"F2.opExtrude","SWEPT_FACE",FACE,{"disambiguationData":[OSD([subQ5])]})])],"derivedFrom":makeQuery(id+"F3.boolean.opBoolean","COPY",FACE,{"derivedFrom":makeQuery(id+"F3.opExtrude","CAP_FACE",FACE,{"disambiguationData":[OSD([subQ5,subQ1,subQ6,subQ7,subQ4,subQ3,subQ2,subQ0])],"isStart":false})})}),makeQuery(id+"F8.opExtrude","SWEPT_FACE",FACE,{"disambiguationData":[OSD([sQuery(id+"F7.wireOp",EDGE,"E67")])]})]});}
            var Q5;
            Q5=makeQuery(id+"F8.boolean.opBoolean","INTERSECT",EDGE,{"disambiguationData":[OD(0.0)],"derivedFrom":[makeQuery(id+"F5.opExtrude","SWEPT_FACE",FACE,{"disambiguationData":[OSD([sQuery(id+"F4.wireOp",EDGE,"E30")])]}),makeQuery(id+"F8.opExtrude","SWEPT_FACE",FACE,{"disambiguationData":[OSD([sQuery(id+"F7.wireOp",EDGE,"E67")])]})]});
            fillet(context, id + "F14", {"entities" : qUnion([Q0, Q1, Q2, Q3, Q4, Q5]), "radius" : 3 * mm, "tangentPropagation" : true, "allowEdgeOverflow" : false});
        }
        {
            var Q0;
            Q0=makeQuery(id+"F1.opExtrude","CAP_EDGE",EDGE,{"disambiguationData":[OSD([sQuery(id+"F0.wireOp",EDGE,"E1.bottom")])],"isStart":false});
            fillet(context, id + "F15", {"entities" : qUnion([Q0]), "radius" : 2 * mm, "tangentPropagation" : true, "allowEdgeOverflow" : false});
        }
        {
            var Q0;
            {var subQ0=sQuery(id+"F0.wireOp",EDGE,"E21.filletArc");var subQ1=sQuery(id+"F0.wireOp",EDGE,"E7");var subQ2=sQuery(id+"F0.wireOp",EDGE,"E6");var subQ3=sQuery(id+"F0.wireOp",EDGE,"E5");var subQ4=sQuery(id+"F0.wireOp",EDGE,"E4");var subQ5=sQuery(id+"F0.wireOp",EDGE,"E22.filletArc");var subQ6=sQuery(id+"F0.wireOp",EDGE,"E1.bottom");var subQ7=sQuery(id+"F0.wireOp",EDGE,"E1.right");var subQ8=sQuery(id+"F0.wireOp",EDGE,"E1.top");var subQ9=sQuery(id+"F0.wireOp",EDGE,"E1.left");var subQ10=sQuery(id+"F0.wireOp",EDGE,"E23.filletArc");var subQ11=sQuery(id+"F0.wireOp",EDGE,"E24.filletArc");Q0=makeQuery(id+"F2.boolean.opBoolean","SPLIT",FACE,{"disambiguationData":[TD([makeQuery(id+"F1.opExtrude","SWEPT_FACE",FACE,{"disambiguationData":[OSD([subQ6])]})])],"derivedFrom":makeQuery(id+"F1.opExtrude","CAP_FACE",FACE,{"disambiguationData":[OSD([subQ6,subQ8,subQ9,subQ7,subQ4,subQ3,subQ2,subQ1,subQ0,subQ5,subQ10,subQ11])],"isStart":true})});}
            var sketch = newSketch(context, id + "F16", { "sketchPlane" : qUnion([Q0])});
            skLineSegment(sketch, "E79", {"start": v(0, 90) * mm, "end": v(0, 120) * mm, "construction": true});
            skCircle(sketch, "E80", {"center": v(0, 120) * mm, "radius": 6 * mm});
            skArc(sketch, "E81", {"start": v(15, 120) * mm, "mid": v(0, 135) * mm, "end": v(-15, 120) * mm});
            skLineSegment(sketch, "E82", {"start": v(-15, 120) * mm, "end": v(-15, 108) * mm});
            skLineSegment(sketch, "E83", {"start": v(-15, 108) * mm, "end": v(-33, 90) * mm});
            skLineSegment(sketch, "E84", {"start": v(15, 120) * mm, "end": v(15, 108) * mm});
            skLineSegment(sketch, "E85", {"start": v(15, 108) * mm, "end": v(33, 90) * mm});
            skLineSegment(sketch, "E86", {"start": v(-80, 0) * mm, "end": v(80, 0) * mm, "construction": true});
            skCircle(sketch, "E87.MirrorC", {"center": v(0, -120) * mm, "radius": 6 * mm});
            skLineSegment(sketch, "E88.MirrorCS", {"start": v(15, -120) * mm, "end": v(15, -108) * mm});
            skArc(sketch, "E89.MirrorCS", {"start": v(15, -120) * mm, "mid": v(0, -135) * mm, "end": v(-15, -120) * mm});
            skLineSegment(sketch, "E90.MirrorCS", {"start": v(-15, -120) * mm, "end": v(-15, -108) * mm});
            skLineSegment(sketch, "E91.MirrorCS", {"start": v(0, -90) * mm, "end": v(0, -120) * mm, "construction": true});
            skLineSegment(sketch, "E92.MirrorCS", {"start": v(-15, -108) * mm, "end": v(-33, -90) * mm});
            skLineSegment(sketch, "E93.MirrorCS", {"start": v(15, -108) * mm, "end": v(33, -90) * mm});
            skSolve(sketch);
        }
        {
            var Q0;
            Q0=makeQuery(id+"F16.imprint","IMPRINT",FACE,{"disambiguationData":[TD([[makeQuery(id+"F16.imprint","IMPRINT",EDGE,{"derivedFrom":sQuery(id+"F16.wireOp",EDGE,"E80")}),-1.0]])]});
            var Q1;
            Q1=makeQuery(id+"F16.imprint","IMPRINT",FACE,{"disambiguationData":[TD([[makeQuery(id+"F16.imprint","IMPRINT",EDGE,{"derivedFrom":sQuery(id+"F16.wireOp",EDGE,"E87.MirrorC")}),1.0]])]});
            var Q2;
            Q2=makeQuery(id+"F16.imprint","IMPRINT",FACE,{"disambiguationData":[TD([[makeQuery(id+"F16.imprint","IMPRINT",EDGE,{"derivedFrom":makeQuery(id+"F1.opExtrude","CAP_EDGE",EDGE,{"disambiguationData":[OSD([sQuery(id+"F0.wireOp",EDGE,"E1.left")])],"isStart":true})}),-1.0]])]});
            var Q3;
            Q3=makeQuery(id+"F2.opExtrude","CAP_FACE",FACE,{"disambiguationData":[OSD([sQuery(id+"F0.wireOp",EDGE,"E12"),sQuery(id+"F0.wireOp",EDGE,"E13"),sQuery(id+"F0.wireOp",EDGE,"E14"),sQuery(id+"F0.wireOp",EDGE,"E15"),sQuery(id+"F0.wireOp",EDGE,"E17.filletArc"),sQuery(id+"F0.wireOp",EDGE,"E18.filletArc"),sQuery(id+"F0.wireOp",EDGE,"E19.filletArc"),sQuery(id+"F0.wireOp",EDGE,"E20.filletArc"),sQuery(id+"F0.wireOp",EDGE,"E25.0"),sQuery(id+"F0.wireOp",EDGE,"E25.1"),sQuery(id+"F0.wireOp",EDGE,"E25.2"),sQuery(id+"F0.wireOp",EDGE,"E25.3"),sQuery(id+"F0.wireOp",EDGE,"E25.4"),sQuery(id+"F0.wireOp",EDGE,"E25.5"),sQuery(id+"F0.wireOp",EDGE,"E25.6"),sQuery(id+"F0.wireOp",EDGE,"E25.7")])],"isStart":false});
            extrude(context, id + "F17", {"entities" : qUnion([Q0, Q1, Q2]), "endBound" : BoundingType.UP_TO_SURFACE, "depth" : 25 * mm, "endBoundEntityFace" : qUnion([Q3]), "offsetDistance" : 25 * mm});
        }
    });
